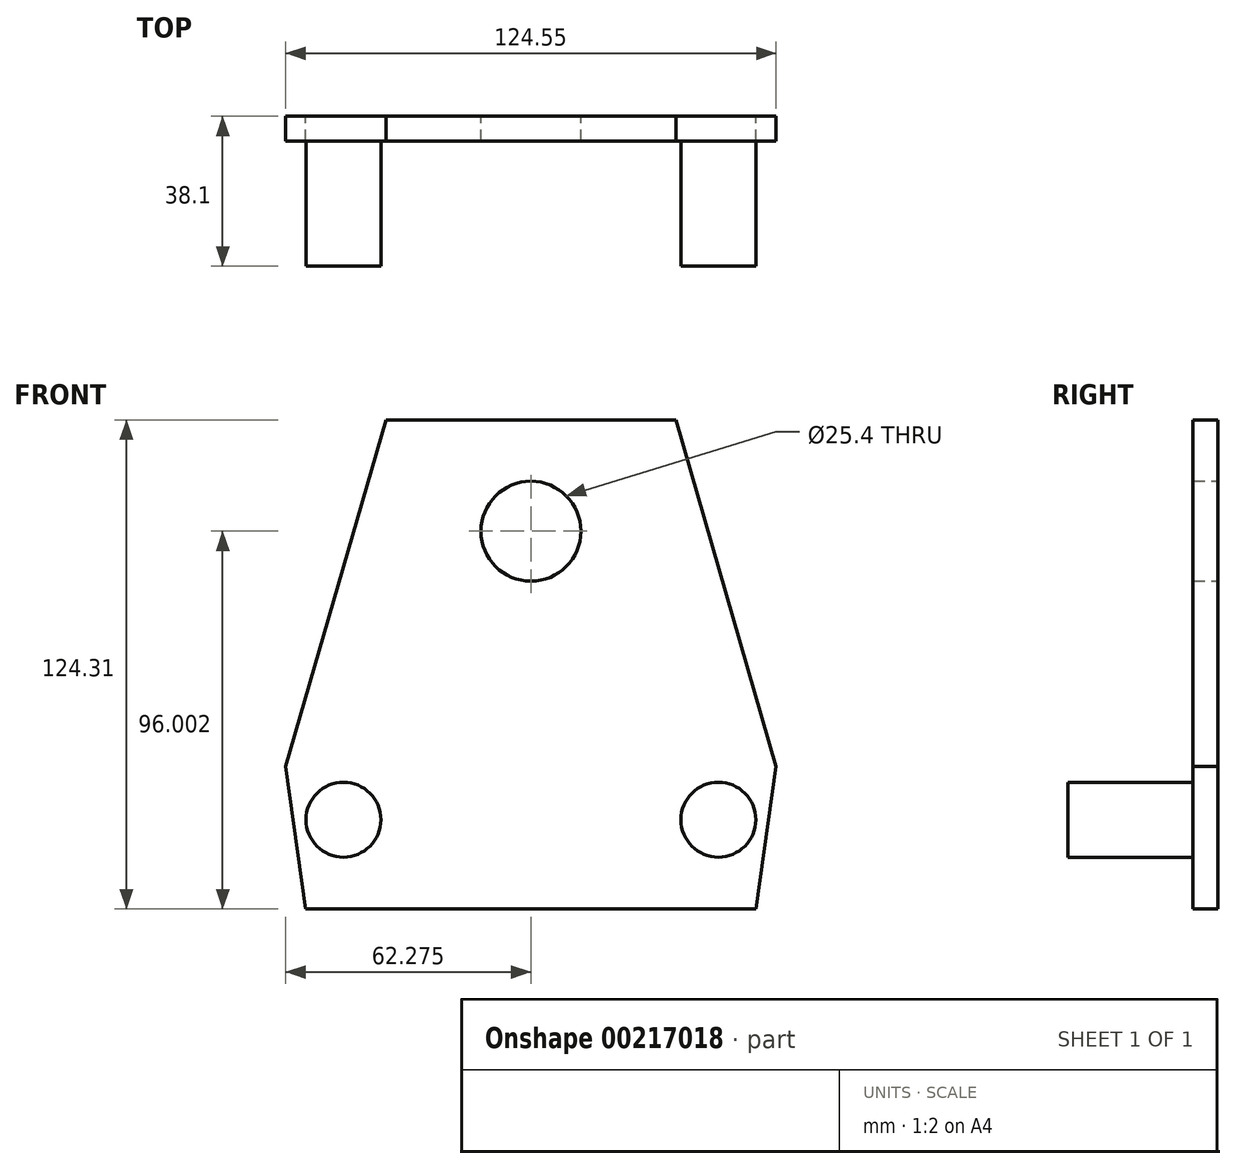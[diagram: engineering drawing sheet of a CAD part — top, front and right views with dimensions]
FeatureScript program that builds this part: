
annotation { "Feature Type Name" : "Feature", "Feature Type Description" : "" }
export const myFeature = defineFeature(function(context is Context, id is Id, definition is map)
    precondition{}
    {
        {
            var Q0;
            Q0=qCreatedBy(makeId("Front.planeOp"),FACE);
            var sketch = newSketch(context, id + "F0", { "sketchPlane" : qUnion([Q0])});
            skLineSegment(sketch, "E0", {"start": v(0, 0) * mm, "end": v(-95.25, 0) * mm, "construction": true});
            skCircle(sketch, "E1", {"center": v(-95.25, 0) * mm, "radius": 9.53 * mm});
            skCircle(sketch, "E2", {"center": v(0, 0) * mm, "radius": 9.53 * mm});
            skLineSegment(sketch, "E3", {"start": v(-47.63, 0) * mm, "end": v(-47.63, 101.6) * mm});
            skLineSegment(sketch, "E4", {"start": v(-47.63, 101.6) * mm, "end": v(-84.47, 101.6) * mm});
            skLineSegment(sketch, "E5", {"start": v(-84.47, 101.6) * mm, "end": v(-109.9, 13.53) * mm});
            skLineSegment(sketch, "E6", {"start": v(-109.9, 13.53) * mm, "end": v(-104.82, -22.7) * mm});
            skLineSegment(sketch, "E7", {"start": v(-104.82, -22.7) * mm, "end": v(19.16, -22.7) * mm});
            skLineSegment(sketch, "E8.MirrorCS", {"start": v(-47.63, 101.6) * mm, "end": v(-10.78, 101.6) * mm});
            skLineSegment(sketch, "E9.MirrorCS", {"start": v(-10.78, 101.6) * mm, "end": v(14.65, 13.53) * mm});
            skLineSegment(sketch, "E10.MirrorCS", {"start": v(14.65, 13.53) * mm, "end": v(9.57, -22.7) * mm});
            skCircle(sketch, "E11", {"center": v(-47.63, 73.3) * mm, "radius": 12.7 * mm});
            skSolve(sketch);
        }
        {
            var Q0;
            Q0 = qSketchRegion(id + "F0", true);
            extrude(context, id + "F1", {"entities" : qUnion([Q0]), "depth" : 6.35 * mm});
        }
        {
            var Q0;
            Q0=makeQuery(id+"F0.imprint","IMPRINT",FACE,{"disambiguationData":[TD([[makeQuery(id+"F0.imprint","IMPRINT",EDGE,{"derivedFrom":sQuery(id+"F0.wireOp",EDGE,"E1")}),1.0]])]});
            var Q1;
            Q1=makeQuery(id+"F0.imprint","IMPRINT",FACE,{"disambiguationData":[TD([[makeQuery(id+"F0.imprint","IMPRINT",EDGE,{"derivedFrom":sQuery(id+"F0.wireOp",EDGE,"E2")}),1.0]])]});
            extrude(context, id + "F2", {"entities" : qUnion([Q0, Q1]), "operationType" : NewBodyOperationType.ADD, "depth" : 38.1 * mm});
        }
    });
